MODEL slx_d316ca5214d0
CONFIG AbsTol = auto
CONFIG FixedStep = 0.01
CONFIG MaxStep = auto
CONFIG MinStep = auto
CONFIG RelTol = 1e-3
CONFIG SampleTimeConstraint = Unconstrained
CONFIG Solver = FixedStepAuto
CONFIG SolverMode = Auto
CONFIG SolverName = FixedStepAuto
CONFIG StartTime = 0.0
CONFIG StopTime = 10.0
BLOCK [RelationalOperator] Relational Operator
  InputSameDT = off
  Operator = ~=
  OutDataTypeStr = boolean
  Ports = [2, 1]
BLOCK [Scope] Scope
  NumInputPorts = 2
  Ports = [2]
  ScopeSpecificationString = Simulink.scopes.TimeScopeBlockCfg('CurrentConfiguration', extmgr.ConfigurationSet(extmgr.Configuration('Core','General UI',true),extmgr.Configuration('Core','Source UI',true),extmgr.Configuration('Sources','WiredSimulink',true,'DataLoggingSaveFormat','StructureWithTime','DataLoggingLimitDataPoints',true,'DataLoggingDecimation','1','DataLoggingDecimateData',true),extmgr.Configuration('Visuals','Tim...<+2349ch>
BLOCK [SubSystem] Signal Builder
  ClipboardFcn = sigbuilder_block('clipboard');
  CloseFcn = sigbuilder_block('close');
  ContinueFcn = sigbuilder_block('continue');
  CopyFcn = sigbuilder_block('copy');
  DeleteFcn = sigbuilder_block('delete');
  LoadFcn = sigbuilder_block('load');
  MaskHideContents = on
  ModelCloseFcn = sigbuilder_block('modelClose');
  NameChangeFcn = sigbuilder_block('namechange');
  OpenFcn = sigbuilder_block('open',[437.25 117.75 550.5 393 ]);
  PauseFcn = sigbuilder_block('pause');
  Ports = [0, 1]
  PreSaveFcn = sigbuilder_block('preSave');
  RequestExecContextInheritance = off
  StartFcn = sigbuilder_block('start');
  StopFcn = sigbuilder_block('stop');
  Tag = STV Subsys
  Variant = off
BLOCK [Demux] Signal Builder/Demux
  Outputs = 1
  Ports = [1, 1]
  Tag = STV Demux
BLOCK [FromWorkspace] Signal Builder/FromWs
  SampleTime = 0
  Tag = STV FromWs
  VariableName = tuvar
  ZeroCross = on
BLOCK [Outport] Signal Builder/Signal 1
  IconDisplay = Port number
  Tag = STV Outport
BLOCK [UnitDelay] Unit Delay
  InputProcessing = Elements as channels (sample based)
  SampleTime = -1
LINE Relational Operator:1 -> Scope:2
LINE Signal Builder:1 -> Relational Operator:1
LINE Signal Builder:1 -> Scope:1
LINE Signal Builder:1 -> Unit Delay:1
LINE Unit Delay:1 -> Relational Operator:2
